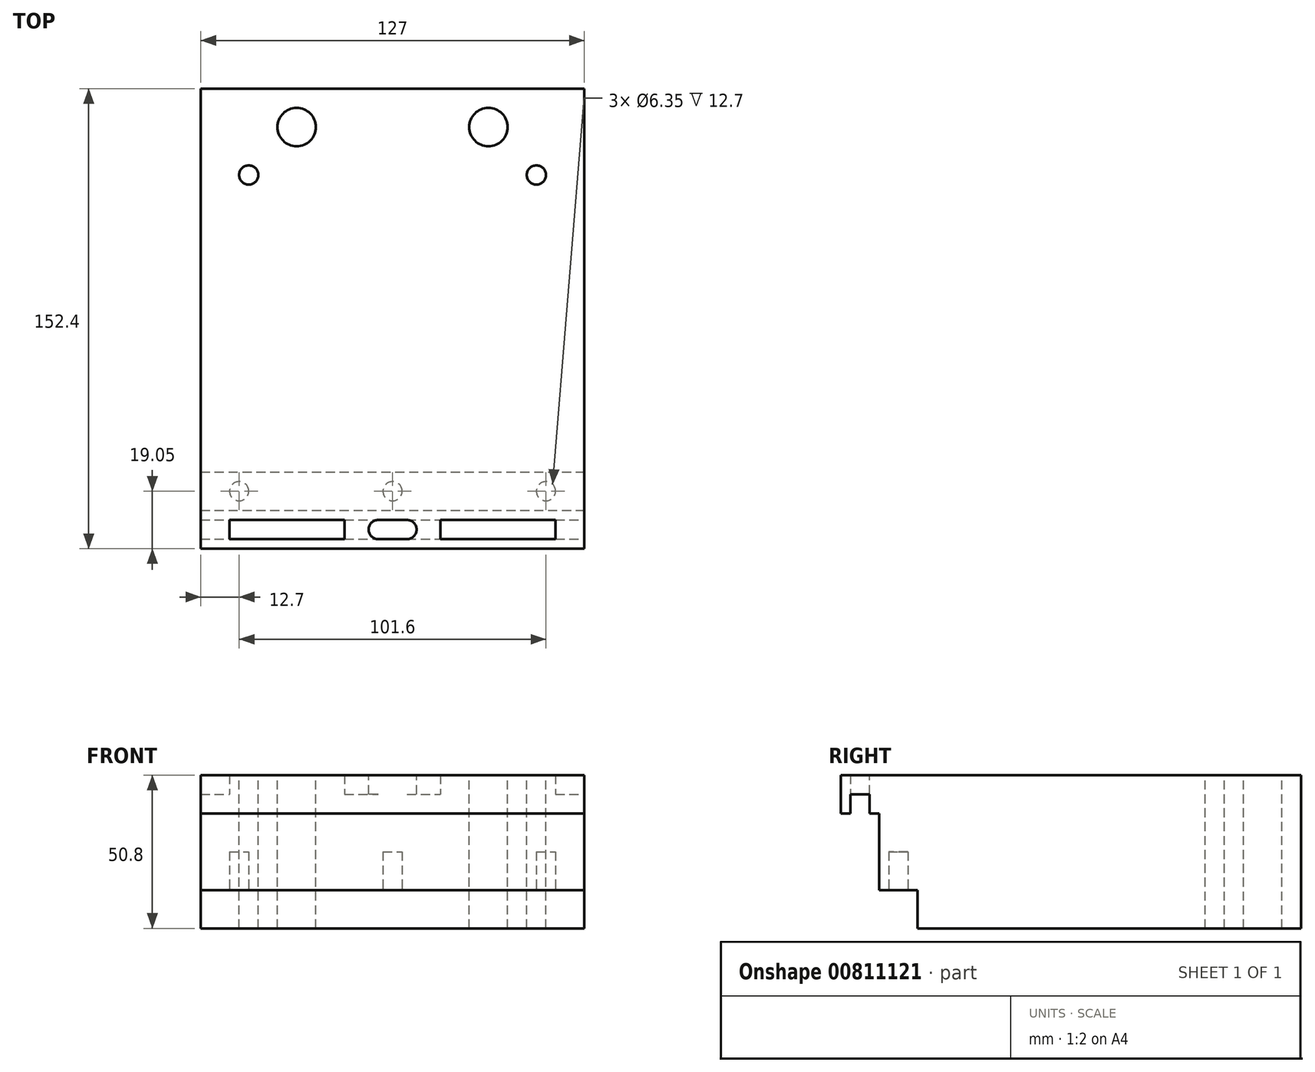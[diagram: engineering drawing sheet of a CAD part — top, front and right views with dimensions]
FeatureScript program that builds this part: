
annotation { "Feature Type Name" : "Feature", "Feature Type Description" : "" }
export const myFeature = defineFeature(function(context is Context, id is Id, definition is map)
    precondition{}
    {
        {
            var Q0;
            Q0=qCreatedBy(makeId("Top.planeOp"),FACE);
            var sketch = newSketch(context, id + "F0", { "sketchPlane" : qUnion([Q0])});
            skLineSegment(sketch, "E0.bottom", {"start": v(63.5, -76.2) * mm, "end": v(-63.5, -76.2) * mm});
            skLineSegment(sketch, "E0.top", {"start": v(63.5, 76.2) * mm, "end": v(-63.5, 76.2) * mm});
            skLineSegment(sketch, "E0.left", {"start": v(63.5, -76.2) * mm, "end": v(63.5, 76.2) * mm});
            skLineSegment(sketch, "E0.right", {"start": v(-63.5, -76.2) * mm, "end": v(-63.5, 76.2) * mm});
            skPoint(sketch, "E0.middle", {"position": v(0, 0) * mm});
            skSolve(sketch);
        }
        {
            var Q0;
            Q0 = qSketchRegion(id + "F0", true);
            extrude(context, id + "F1", {"entities" : qUnion([Q0]), "oppositeDirection" : true, "depth" : 50.8 * mm, "offsetDistance" : 25.4 * mm});
        }
        {
            var Q0;
            Q0=makeQuery(id+"F1.opExtrude","SWEPT_FACE",FACE,{"disambiguationData":[OSD([sQuery(id+"F0.wireOp",EDGE,"E0.left")])]});
            var sketch = newSketch(context, id + "F2", { "sketchPlane" : qUnion([Q0])});
            skLineSegment(sketch, "E1", {"start": v(-76.2, -50.8) * mm, "end": v(-50.8, -50.8) * mm});
            skLineSegment(sketch, "E2", {"start": v(-50.8, -50.8) * mm, "end": v(-50.8, -38.1) * mm});
            skLineSegment(sketch, "E3", {"start": v(-50.8, -38.1) * mm, "end": v(-63.5, -38.1) * mm});
            skLineSegment(sketch, "E4", {"start": v(-63.5, -38.1) * mm, "end": v(-63.5, -12.7) * mm});
            skLineSegment(sketch, "E5", {"start": v(-63.5, -12.7) * mm, "end": v(-66.67, -12.7) * mm});
            skLineSegment(sketch, "E6", {"start": v(-76.2, -12.7) * mm, "end": v(-76.2, -50.8) * mm});
            skLineSegment(sketch, "E7", {"start": v(-66.67, -6.35) * mm, "end": v(-73.02, -6.35) * mm});
            skLineSegment(sketch, "E8", {"start": v(-73.02, -6.35) * mm, "end": v(-73.02, -12.7) * mm});
            skLineSegment(sketch, "E9", {"start": v(-66.67, -6.35) * mm, "end": v(-66.67, -12.7) * mm});
            skLineSegment(sketch, "E10.trimOffspring", {"start": v(-73.02, -12.7) * mm, "end": v(-76.2, -12.7) * mm});
            skSolve(sketch);
        }
        {
            var Q0;
            Q0 = qSketchRegion(id + "F2", true);
            extrude(context, id + "F3", {"entities" : qUnion([Q0]), "operationType" : NewBodyOperationType.REMOVE, "endBound" : BoundingType.THROUGH_ALL, "oppositeDirection" : true, "depth" : 25.4 * mm, "offsetDistance" : 25.4 * mm});
        }
        {
            var Q0;
            Q0=makeQuery(id+"F3.boolean.opBoolean","COPY",FACE,{"derivedFrom":makeQuery(id+"F3.opExtrude","SWEPT_FACE",FACE,{"disambiguationData":[OSD([sQuery(id+"F2.wireOp",EDGE,"E3")])]})});
            var sketch = newSketch(context, id + "F4", { "sketchPlane" : qUnion([Q0])});
            skLineSegment(sketch, "E11", {"start": v(-63.5, 57.15) * mm, "end": v(63.5, 57.15) * mm});
            skCircle(sketch, "E12", {"center": v(0, 57.15) * mm, "radius": 3.18 * mm});
            skCircle(sketch, "E13", {"center": v(50.8, 57.15) * mm, "radius": 3.18 * mm});
            skCircle(sketch, "E14", {"center": v(-50.8, 57.15) * mm, "radius": 3.18 * mm});
            skSolve(sketch);
        }
        {
            var Q0;
            Q0 = qSketchRegion(id + "F4", true);
            extrude(context, id + "F5", {"entities" : qUnion([Q0]), "operationType" : NewBodyOperationType.REMOVE, "oppositeDirection" : true, "depth" : 12.7 * mm, "offsetDistance" : 25.4 * mm});
        }
        {
            var Q0;
            Q0=makeQuery(id+"F3.boolean.opBoolean","COPY",FACE,{"derivedFrom":makeQuery(id+"F3.opExtrude","SWEPT_FACE",FACE,{"disambiguationData":[OSD([sQuery(id+"F2.wireOp",EDGE,"E7")])]})});
            var sketch = newSketch(context, id + "F6", { "sketchPlane" : qUnion([Q0])});
            skLineSegment(sketch, "E15.0", {"start": v(-53.97, 73.02) * mm, "end": v(-15.88, 73.02) * mm});
            skLineSegment(sketch, "E15.1", {"start": v(-53.97, 66.67) * mm, "end": v(-15.88, 66.67) * mm});
            skLineSegment(sketch, "E16.0", {"start": v(-15.88, 73.02) * mm, "end": v(-15.88, 66.67) * mm});
            skLineSegment(sketch, "E17.0", {"start": v(15.88, 73.02) * mm, "end": v(15.88, 66.67) * mm});
            skLineSegment(sketch, "E18.0", {"start": v(-53.98, 73.02) * mm, "end": v(-53.98, 66.67) * mm});
            skLineSegment(sketch, "E19.0", {"start": v(53.98, 73.02) * mm, "end": v(53.98, 66.67) * mm});
            skPoint(sketch, "E20.orphan", {"position": v(63.5, 73.02) * mm});
            skPoint(sketch, "E21.orphan", {"position": v(63.5, 66.67) * mm});
            skLineSegment(sketch, "E22.trimOffspring", {"start": v(15.88, 66.67) * mm, "end": v(53.97, 66.67) * mm});
            skLineSegment(sketch, "E23.trimOffspring", {"start": v(15.88, 73.02) * mm, "end": v(53.97, 73.02) * mm});
            skPoint(sketch, "E24.orphan", {"position": v(-63.5, 73.02) * mm});
            skPoint(sketch, "E25.orphan", {"position": v(-63.5, 66.67) * mm});
            skSolve(sketch);
        }
        {
            var Q0;
            Q0 = qSketchRegion(id + "F6", true);
            extrude(context, id + "F7", {"entities" : qUnion([Q0]), "operationType" : NewBodyOperationType.REMOVE, "endBound" : BoundingType.THROUGH_ALL, "oppositeDirection" : true, "depth" : 25.4 * mm, "offsetDistance" : 25.4 * mm});
        }
        {
            var Q0;
            Q0=makeQuery(id+"F1.opExtrude","CAP_FACE",FACE,{"disambiguationData":[OSD([sQuery(id+"F0.wireOp",EDGE,"E0.bottom"),sQuery(id+"F0.wireOp",EDGE,"E0.top"),sQuery(id+"F0.wireOp",EDGE,"E0.left"),sQuery(id+"F0.wireOp",EDGE,"E0.right")])],"isStart":true});
            var sketch = newSketch(context, id + "F8", { "sketchPlane" : qUnion([Q0])});
            skCircle(sketch, "E26", {"center": v(-31.75, 63.5) * mm, "radius": 6.35 * mm});
            skCircle(sketch, "E27", {"center": v(31.75, 63.5) * mm, "radius": 6.35 * mm});
            skLineSegment(sketch, "E28", {"start": v(-31.75, 63.5) * mm, "end": v(-63.5, 63.5) * mm});
            skLineSegment(sketch, "E29", {"start": v(31.75, 63.5) * mm, "end": v(63.5, 63.5) * mm});
            skLineSegment(sketch, "E30", {"start": v(-47.62, 63.5) * mm, "end": v(-47.62, 47.62) * mm});
            skLineSegment(sketch, "E31", {"start": v(47.62, 63.5) * mm, "end": v(47.62, 47.62) * mm});
            skCircle(sketch, "E32", {"center": v(-47.62, 47.62) * mm, "radius": 3.18 * mm});
            skCircle(sketch, "E33", {"center": v(47.62, 47.62) * mm, "radius": 3.18 * mm});
            skSolve(sketch);
        }
        {
            var Q0;
            Q0 = qSketchRegion(id + "F8", true);
            extrude(context, id + "F9", {"entities" : qUnion([Q0]), "operationType" : NewBodyOperationType.REMOVE, "endBound" : BoundingType.THROUGH_ALL, "oppositeDirection" : true, "depth" : 25.4 * mm, "offsetDistance" : 25.4 * mm});
        }
        {
            var Q0;
            Q0=makeQuery(id+"F1.opExtrude","CAP_FACE",FACE,{"disambiguationData":[OSD([sQuery(id+"F0.wireOp",EDGE,"E0.bottom"),sQuery(id+"F0.wireOp",EDGE,"E0.top"),sQuery(id+"F0.wireOp",EDGE,"E0.left"),sQuery(id+"F0.wireOp",EDGE,"E0.right")])],"isStart":true});
            var sketch = newSketch(context, id + "F10", { "sketchPlane" : qUnion([Q0])});
            skLineSegment(sketch, "E34.0", {"start": v(63.5, -76.2) * mm, "end": v(-63.5, -76.2) * mm});
            skPoint(sketch, "E35.endSnap0", {"position": v(15.88, -69.85) * mm});
            skArc(sketch, "E36", {"start": v(-4.76, -66.67) * mm, "mid": v(-7.94, -69.85) * mm, "end": v(-4.76, -73.02) * mm});
            skArc(sketch, "E37", {"start": v(4.76, -73.02) * mm, "mid": v(7.94, -69.85) * mm, "end": v(4.76, -66.67) * mm});
            skLineSegment(sketch, "E38", {"start": v(-4.76, -73.02) * mm, "end": v(4.76, -73.02) * mm});
            skLineSegment(sketch, "E39", {"start": v(-4.76, -66.67) * mm, "end": v(4.76, -66.67) * mm});
            skSolve(sketch);
        }
        {
            var Q0;
            Q0 = qSketchRegion(id + "F10", true);
            extrude(context, id + "F11", {"entities" : qUnion([Q0]), "operationType" : NewBodyOperationType.REMOVE, "endBound" : BoundingType.THROUGH_ALL, "oppositeDirection" : true, "depth" : 25.4 * mm, "offsetDistance" : 25.4 * mm});
        }
    });
